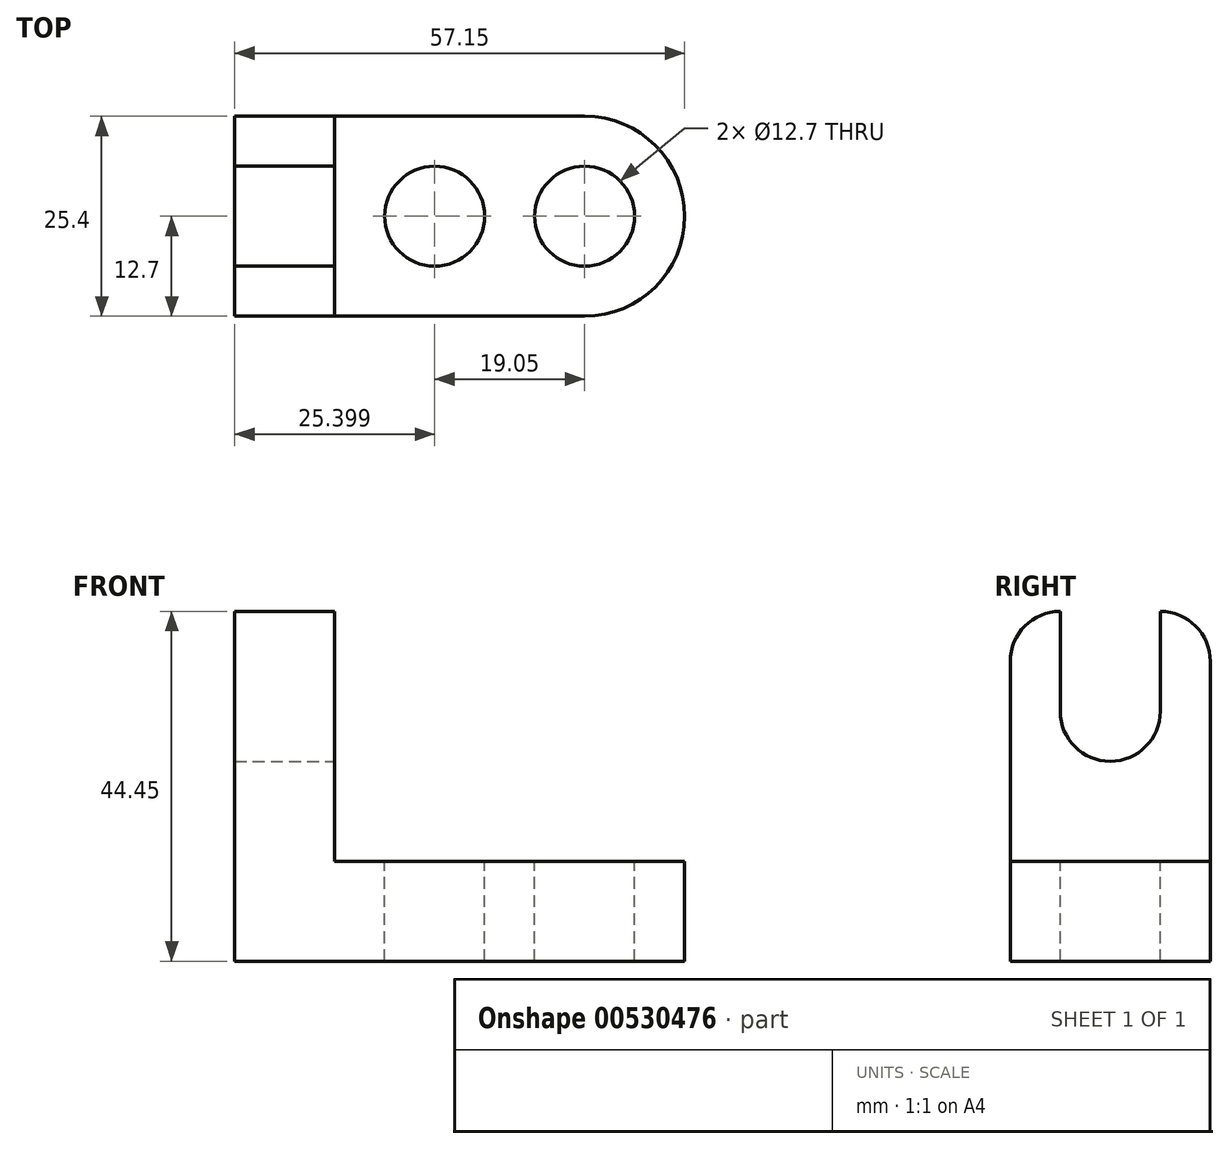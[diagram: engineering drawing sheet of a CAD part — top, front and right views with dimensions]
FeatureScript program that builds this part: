
annotation { "Feature Type Name" : "Feature", "Feature Type Description" : "" }
export const myFeature = defineFeature(function(context is Context, id is Id, definition is map)
    precondition{}
    {
        {
            var Q0;
            Q0=qCreatedBy(makeId("Front.planeOp"),FACE);
            var sketch = newSketch(context, id + "F0", { "sketchPlane" : qUnion([Q0])});
            skLineSegment(sketch, "E0", {"start": v(-72.07, 44.45) * mm, "end": v(-72.07, 0) * mm});
            skLineSegment(sketch, "E1", {"start": v(-72.07, 0) * mm, "end": v(-14.92, 0) * mm});
            skLineSegment(sketch, "E2", {"start": v(-14.92, 0) * mm, "end": v(-14.92, 12.7) * mm});
            skLineSegment(sketch, "E3", {"start": v(-14.92, 12.7) * mm, "end": v(-59.37, 12.7) * mm});
            skLineSegment(sketch, "E4", {"start": v(-59.37, 12.7) * mm, "end": v(-59.37, 44.45) * mm});
            skLineSegment(sketch, "E5", {"start": v(-59.37, 44.45) * mm, "end": v(-72.07, 44.45) * mm});
            skSolve(sketch);
        }
        {
            var Q0;
            Q0=makeQuery(id+"F0.imprint","IMPRINT",FACE,{"disambiguationData":[TD([[makeQuery(id+"F0.imprint","IMPRINT",EDGE,{"derivedFrom":sQuery(id+"F0.wireOp",EDGE,"E0")}),1.0]])]});
            extrude(context, id + "F1", {"entities" : qUnion([Q0]), "depth" : 25.4 * mm, "offsetDistance" : 25.4 * mm});
        }
        {
            var Q0;
            Q0=makeQuery(id+"F1.opExtrude","SWEPT_FACE",FACE,{"disambiguationData":[OSD([sQuery(id+"F0.wireOp",EDGE,"E4")])]});
            var sketch = newSketch(context, id + "F2", { "sketchPlane" : qUnion([Q0])});
            skCircle(sketch, "E6", {"center": v(-12.7, 31.75) * mm, "radius": 6.35 * mm});
            skLineSegment(sketch, "E7", {"start": v(-19.05, 31.75) * mm, "end": v(-19.05, 44.45) * mm});
            skLineSegment(sketch, "E8", {"start": v(-6.35, 31.75) * mm, "end": v(-6.35, 44.45) * mm});
            skLineSegment(sketch, "E9", {"start": v(-6.35, 44.45) * mm, "end": v(-19.05, 44.45) * mm});
            skSolve(sketch);
        }
        {
            var Q0;
            {var subQ0=sQuery(id+"F2.wireOp",EDGE,"E7");Q0=makeQuery(id+"F2.imprint","IMPRINT",FACE,{"disambiguationData":[TD([[makeQuery(id+"F2.imprint","IMPRINT",EDGE,{"derivedFrom":subQ0}),-1.0]])]});}
            var Q1;
            {var subQ0=sQuery(id+"F2.wireOp",EDGE,"E6");var subQ1=makeQuery(id+"F2.imprint","INTERSECT",VERTEX,{"derivedFrom":[subQ0,sQuery(id+"F2.wireOp",EDGE,"E7")]});Q1=makeQuery(id+"F2.imprint","IMPRINT",FACE,{"disambiguationData":[TD([[makeQuery(id+"F2.imprint","IMPRINT",EDGE,{"disambiguationData":[TD([[subQ1,1.0]])],"derivedFrom":subQ0}),1.0]])]});}
            extrude(context, id + "F3", {"entities" : qUnion([Q0, Q1]), "operationType" : NewBodyOperationType.REMOVE, "oppositeDirection" : true, "depth" : 25.4 * mm, "offsetDistance" : 25.4 * mm});
        }
        {
            var Q0;
            Q0=makeQuery(id+"F1.opExtrude","SWEPT_FACE",FACE,{"disambiguationData":[OSD([sQuery(id+"F0.wireOp",EDGE,"E4")])]});
            var sketch = newSketch(context, id + "F4", { "sketchPlane" : qUnion([Q0])});
            skArc(sketch, "E10", {"start": v(-19.05, 44.45) * mm, "mid": v(-23.54, 42.6) * mm, "end": v(-25.4, 38.1) * mm});
            skPoint(sketch, "E10.endSnap0", {"position": v(-19.05, 38.1) * mm});
            skPoint(sketch, "E11.startSnap0", {"position": v(-6.35, 38.1) * mm});
            skArc(sketch, "E12", {"start": v(0, 38.1) * mm, "mid": v(-1.86, 42.6) * mm, "end": v(-6.35, 44.45) * mm});
            skSolve(sketch);
        }
        {
            var Q0;
            {var subQ1=sQuery(id+"F0.wireOp",EDGE,"E5");var subQ2=sQuery(id+"F0.wireOp",EDGE,"E4");var subQ3=sQuery(id+"F2.wireOp",EDGE,"E7");var subQ4=makeQuery(id+"F3.boolean.opBoolean","SPLIT",EDGE,{"disambiguationData":[TD([makeQuery(id+"F3.opExtrude","SWEPT_FACE",FACE,{"disambiguationData":[OSD([subQ3])]})])],"derivedFrom":makeQuery(id+"F1.opExtrude","SWEPT_EDGE",EDGE,{"disambiguationData":[OSD([subQ2,subQ1])]})});Q0=makeQuery(id+"F4.imprint","IMPRINT",FACE,{"disambiguationData":[TD([[makeQuery(id+"F4.imprint","IMPRINT",EDGE,{"derivedFrom":subQ4}),-1.0]])]});}
            var Q1;
            {var subQ1=sQuery(id+"F0.wireOp",EDGE,"E5");var subQ2=sQuery(id+"F0.wireOp",EDGE,"E4");var subQ3=sQuery(id+"F2.wireOp",EDGE,"E8");var subQ4=makeQuery(id+"F3.boolean.opBoolean","SPLIT",EDGE,{"disambiguationData":[TD([makeQuery(id+"F3.opExtrude","SWEPT_FACE",FACE,{"disambiguationData":[OSD([subQ3])]})])],"derivedFrom":makeQuery(id+"F1.opExtrude","SWEPT_EDGE",EDGE,{"disambiguationData":[OSD([subQ2,subQ1])]})});Q1=makeQuery(id+"F4.imprint","IMPRINT",FACE,{"disambiguationData":[TD([[makeQuery(id+"F4.imprint","IMPRINT",EDGE,{"derivedFrom":subQ4}),-1.0]])]});}
            extrude(context, id + "F5", {"entities" : qUnion([Q0, Q1]), "operationType" : NewBodyOperationType.REMOVE, "oppositeDirection" : true, "depth" : 25.4 * mm, "offsetDistance" : 25.4 * mm});
        }
        {
            var Q0;
            Q0=makeQuery(id+"F1.opExtrude","SWEPT_FACE",FACE,{"disambiguationData":[OSD([sQuery(id+"F0.wireOp",EDGE,"E3")])]});
            var sketch = newSketch(context, id + "F6", { "sketchPlane" : qUnion([Q0])});
            skCircle(sketch, "E13", {"center": v(-46.67, -12.7) * mm, "radius": 6.35 * mm});
            skCircle(sketch, "E14", {"center": v(-27.62, -12.7) * mm, "radius": 6.35 * mm});
            skArc(sketch, "E15", {"start": v(-27.62, -25.4) * mm, "mid": v(-14.92, -12.7) * mm, "end": v(-27.62, 0) * mm});
            skSolve(sketch);
        }
        {
            var Q0;
            Q0 = qSketchRegion(id + "F6", true);
            var Q1;
            {var subQ0=sQuery(id+"F6.wireOp",EDGE,"E15");var subQ1=sQuery(id+"F0.wireOp",EDGE,"E3");var subQ2=makeQuery(id+"F1.opExtrude","CAP_EDGE",EDGE,{"disambiguationData":[OSD([subQ1])],"isStart":true});var subQ3=makeQuery(id+"F6.imprint","INTERSECT",VERTEX,{"derivedFrom":[subQ2,subQ0]});Q1=makeQuery(id+"F6.imprint","IMPRINT",FACE,{"disambiguationData":[TD([[makeQuery(id+"F6.imprint","IMPRINT",EDGE,{"disambiguationData":[TD([[subQ3,1.0]])],"derivedFrom":subQ0}),-1.0]])]});}
            var Q2;
            {var subQ0=sQuery(id+"F6.wireOp",EDGE,"E15");var subQ1=sQuery(id+"F0.wireOp",EDGE,"E3");var subQ2=makeQuery(id+"F1.opExtrude","CAP_EDGE",EDGE,{"disambiguationData":[OSD([subQ1])],"isStart":false});var subQ3=makeQuery(id+"F6.imprint","INTERSECT",VERTEX,{"derivedFrom":[subQ2,subQ0]});Q2=makeQuery(id+"F6.imprint","IMPRINT",FACE,{"disambiguationData":[TD([[makeQuery(id+"F6.imprint","IMPRINT",EDGE,{"disambiguationData":[TD([[subQ3,-1.0]])],"derivedFrom":subQ0}),-1.0]])]});}
            extrude(context, id + "F7", {"entities" : qUnion([Q0, Q1, Q2]), "operationType" : NewBodyOperationType.REMOVE, "oppositeDirection" : true, "depth" : 25.4 * mm, "offsetDistance" : 25.4 * mm});
        }
    });
